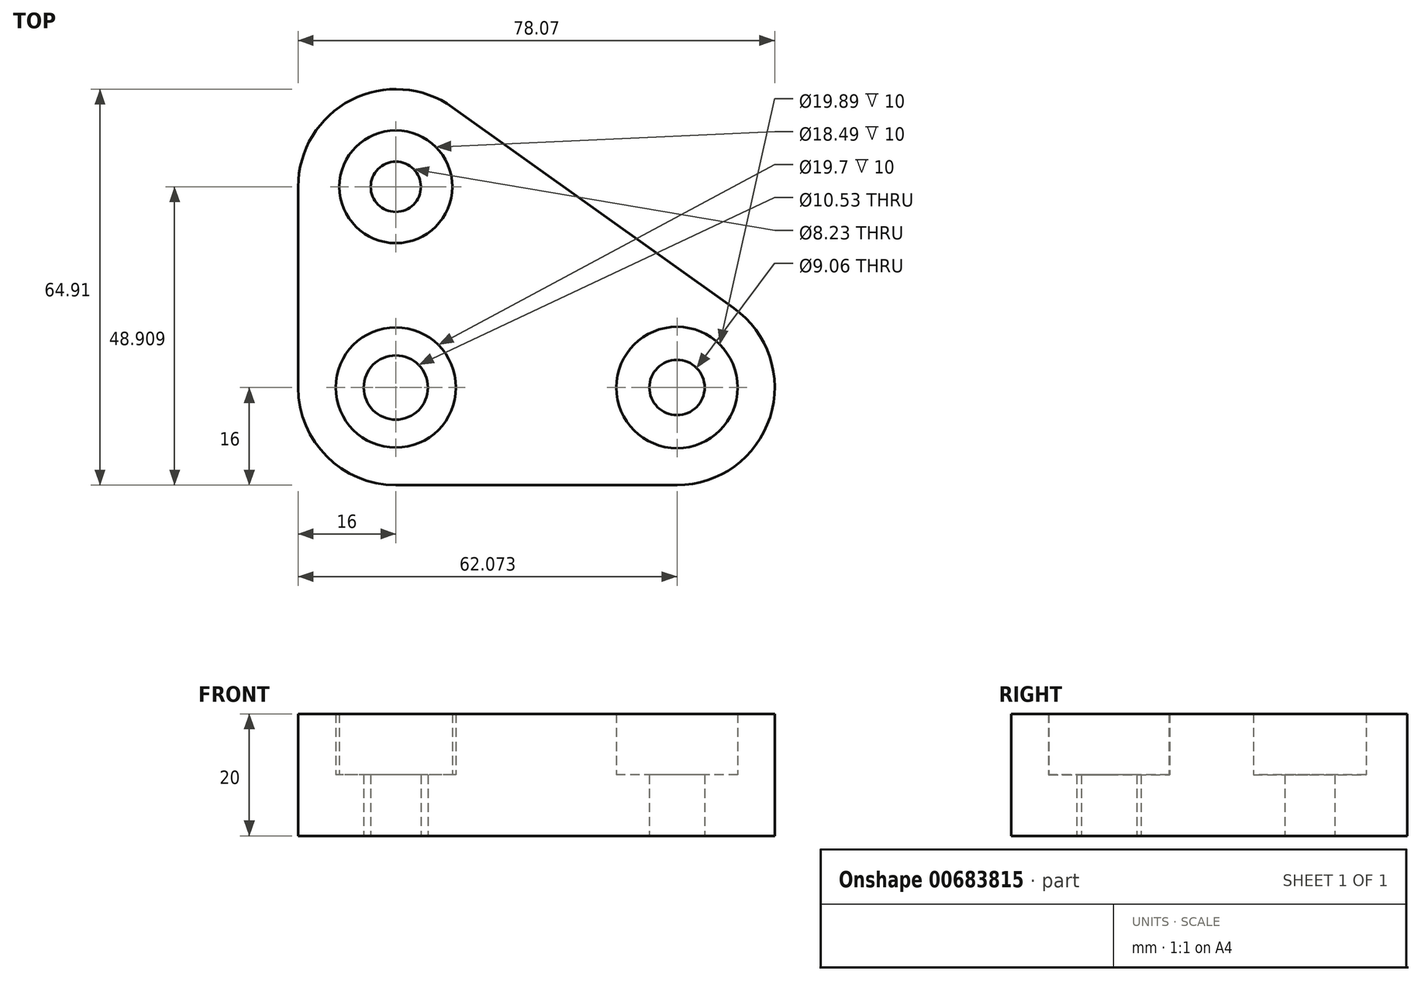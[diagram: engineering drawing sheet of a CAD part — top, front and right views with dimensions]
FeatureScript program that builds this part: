
annotation { "Feature Type Name" : "Feature", "Feature Type Description" : "" }
export const myFeature = defineFeature(function(context is Context, id is Id, definition is map)
    precondition{}
    {
        {
            var Q0;
            Q0=qCreatedBy(makeId("Top.planeOp"),FACE);
            var sketch = newSketch(context, id + "F0", { "sketchPlane" : qUnion([Q0])});
            skLineSegment(sketch, "E0.bottom", {"start": v(16, 0) * mm, "end": v(62.07, 0) * mm});
            skLineSegment(sketch, "E0.left", {"start": v(0, 16) * mm, "end": v(0, 48.9) * mm});
            skLineSegment(sketch, "E1", {"start": v(25.3, 61.93) * mm, "end": v(71.37, 29.02) * mm});
            skPoint(sketch, "E2.visualSharp", {"position": v(0, 80) * mm});
            skArc(sketch, "E2.filletArc", {"start": v(25.3, 61.93) * mm, "mid": v(8.68, 63.14) * mm, "end": v(0, 48.9) * mm});
            skPoint(sketch, "E3.visualSharp", {"position": v(112, 0) * mm});
            skArc(sketch, "E3.filletArc", {"start": v(62.07, 0) * mm, "mid": v(77.3, 11.12) * mm, "end": v(71.37, 29.02) * mm});
            skPoint(sketch, "E4.visualSharp", {"position": v(0, 0) * mm});
            skArc(sketch, "E4.filletArc", {"start": v(0, 16) * mm, "mid": v(4.69, 4.69) * mm, "end": v(16, 0) * mm});
            skCircle(sketch, "E5", {"center": v(16, 48.9) * mm, "radius": 4.12 * mm});
            skCircle(sketch, "E6", {"center": v(16, 48.9) * mm, "radius": 9.25 * mm});
            skCircle(sketch, "E7", {"center": v(62.07, 16) * mm, "radius": 4.53 * mm});
            skCircle(sketch, "E8", {"center": v(62.07, 16) * mm, "radius": 9.95 * mm});
            skCircle(sketch, "E9", {"center": v(16, 16) * mm, "radius": 5.26 * mm});
            skCircle(sketch, "E10", {"center": v(16, 16) * mm, "radius": 9.85 * mm});
            skSolve(sketch);
        }
        {
            var Q0;
            Q0=makeQuery(id+"F0.imprint","IMPRINT",FACE,{"disambiguationData":[TD([[makeQuery(id+"F0.imprint","IMPRINT",EDGE,{"derivedFrom":sQuery(id+"F0.wireOp",EDGE,"E0.bottom")}),1.0]])]});
            extrude(context, id + "F1", {"entities" : qUnion([Q0]), "depth" : 20 * mm, "offsetDistance" : 25 * mm});
        }
        {
            var Q0;
            Q0 = qSketchRegion(id + "F0", true);
            var Q1;
            Q1=makeQuery(id+"F0.imprint","IMPRINT",FACE,{"disambiguationData":[TD([[makeQuery(id+"F0.imprint","IMPRINT",EDGE,{"derivedFrom":sQuery(id+"F0.wireOp",EDGE,"E5")}),-1.0]])]});
            var Q2;
            Q2=makeQuery(id+"F0.imprint","IMPRINT",FACE,{"disambiguationData":[TD([[makeQuery(id+"F0.imprint","IMPRINT",EDGE,{"derivedFrom":sQuery(id+"F0.wireOp",EDGE,"E9")}),-1.0]])]});
            var Q3;
            Q3=makeQuery(id+"F0.imprint","IMPRINT",FACE,{"disambiguationData":[TD([[makeQuery(id+"F0.imprint","IMPRINT",EDGE,{"derivedFrom":sQuery(id+"F0.wireOp",EDGE,"E7")}),-1.0]])]});
            extrude(context, id + "F2", {"entities" : qUnion([Q0, Q1, Q2, Q3]), "operationType" : NewBodyOperationType.ADD, "depth" : 10 * mm, "offsetDistance" : 25 * mm});
        }
    });
